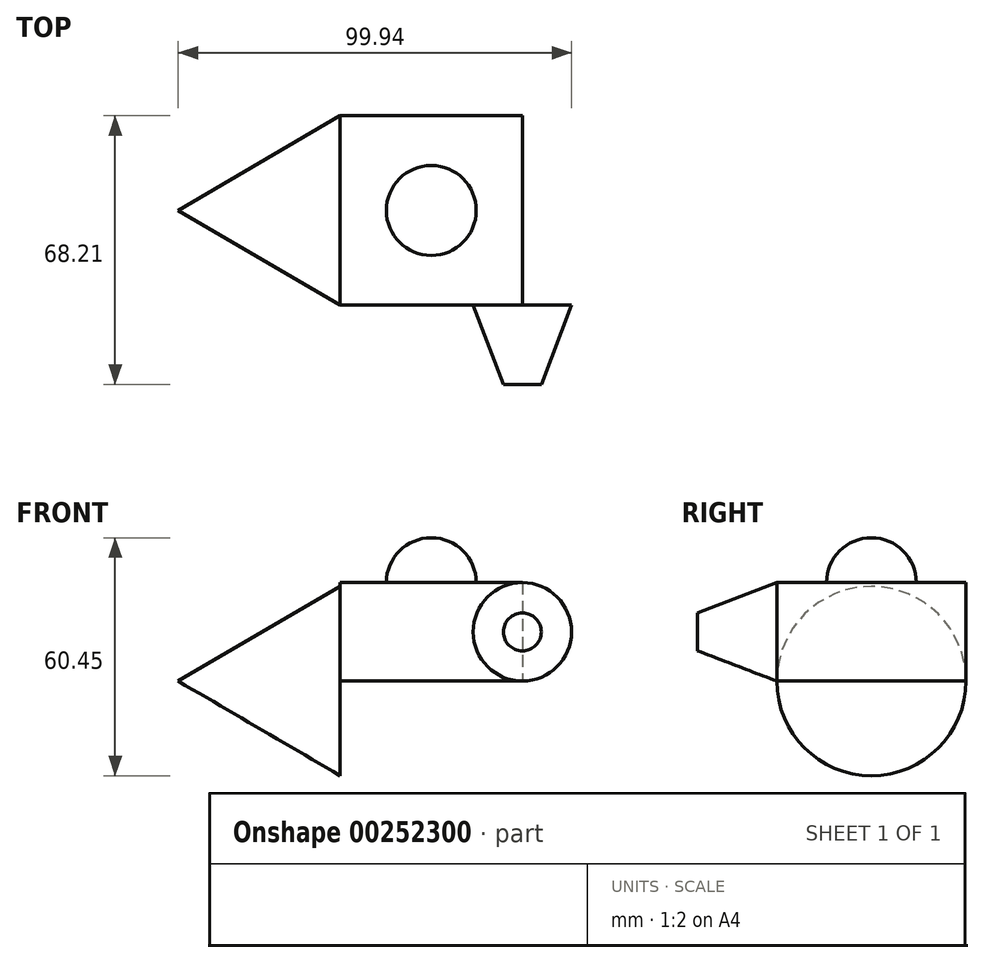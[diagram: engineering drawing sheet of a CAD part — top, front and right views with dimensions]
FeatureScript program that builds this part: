
annotation { "Feature Type Name" : "Feature", "Feature Type Description" : "" }
export const myFeature = defineFeature(function(context is Context, id is Id, definition is map)
    precondition{}
    {
        {
            var Q0;
            Q0=qCreatedBy(makeId("Top.planeOp"),FACE);
            var sketch = newSketch(context, id + "F0", { "sketchPlane" : qUnion([Q0])});
            skLineSegment(sketch, "E0.bottom", {"start": v(-23.14, 24.04) * mm, "end": v(23.14, 24.04) * mm});
            skLineSegment(sketch, "E0.top", {"start": v(-23.14, -24.04) * mm, "end": v(23.14, -24.04) * mm});
            skLineSegment(sketch, "E0.left", {"start": v(-23.14, 24.04) * mm, "end": v(-23.14, -24.04) * mm});
            skLineSegment(sketch, "E0.right", {"start": v(23.14, 24.04) * mm, "end": v(23.14, -24.04) * mm});
            skPoint(sketch, "E0.middle", {"position": v(0, 0) * mm});
            skSolve(sketch);
        }
        {
            var Q0;
            Q0=makeQuery(id+"F0.imprint","IMPRINT",FACE,{"disambiguationData":[TD([[makeQuery(id+"F0.imprint","IMPRINT",EDGE,{"derivedFrom":sQuery(id+"F0.wireOp",EDGE,"E0.bottom")}),-1.0]])]});
            extrude(context, id + "F1", {"entities" : qUnion([Q0]), "endBound" : BoundingType.SYMMETRIC, "depth" : 25 * mm});
        }
        {
            var Q0;
            Q0=makeQuery(id+"F1.opExtrude","CAP_FACE",FACE,{"disambiguationData":[OSD([sQuery(id+"F0.wireOp",EDGE,"E0.bottom"),sQuery(id+"F0.wireOp",EDGE,"E0.top"),sQuery(id+"F0.wireOp",EDGE,"E0.left"),sQuery(id+"F0.wireOp",EDGE,"E0.right")])],"isStart":false});
            var sketch = newSketch(context, id + "F2", { "sketchPlane" : qUnion([Q0])});
            skArc(sketch, "E1", {"start": v(-11.41, 0) * mm, "mid": v(0, -11.41) * mm, "end": v(11.41, 0) * mm});
            skLineSegment(sketch, "E2", {"start": v(0, 0) * mm, "end": v(11.41, 0) * mm});
            skLineSegment(sketch, "E3", {"start": v(11.41, 0) * mm, "end": v(-11.41, 0) * mm});
            skLineSegment(sketch, "E4", {"start": v(23.14, 0) * mm, "end": v(-23.14, 0) * mm, "construction": true});
            skSolve(sketch);
        }
        {
            var Q0;
            Q0 = qSketchRegion(id + "F2", true);
            var Q1;
            Q1=sQuery(id+"F2.wireOp",EDGE,"E4");
            revolve(context, id + "F3", {"operationType" : NewBodyOperationType.ADD, "entities" : qUnion([Q0]), "axis" : qUnion([Q1]), "revolveType" : RevolveType.FULL});
        }
        {
            var Q0;
            Q0=makeQuery(id+"F1.opExtrude","CAP_FACE",FACE,{"disambiguationData":[OSD([sQuery(id+"F0.wireOp",EDGE,"E0.bottom"),sQuery(id+"F0.wireOp",EDGE,"E0.top"),sQuery(id+"F0.wireOp",EDGE,"E0.left"),sQuery(id+"F0.wireOp",EDGE,"E0.right")])],"isStart":true});
            var sketch = newSketch(context, id + "F4", { "sketchPlane" : qUnion([Q0])});
            skLineSegment(sketch, "E5", {"start": v(-23.14, -24.04) * mm, "end": v(-64.3, 0) * mm});
            skLineSegment(sketch, "E6", {"start": v(-64.3, 0) * mm, "end": v(-23.14, 0) * mm});
            skLineSegment(sketch, "E7", {"start": v(-23.14, 0) * mm, "end": v(-23.14, -24.04) * mm});
            skSolve(sketch);
        }
        {
            var Q0;
            Q0 = qSketchRegion(id + "F4", true);
            var Q1;
            Q1=sQuery(id+"F4.wireOp",EDGE,"E6");
            revolve(context, id + "F5", {"operationType" : NewBodyOperationType.ADD, "entities" : qUnion([Q0]), "axis" : qUnion([Q1]), "revolveType" : RevolveType.FULL});
        }
        {
            var Q0;
            Q0=makeQuery(id+"F1.opExtrude","SWEPT_FACE",FACE,{"disambiguationData":[OSD([sQuery(id+"F0.wireOp",EDGE,"E0.right")])]});
            var sketch = newSketch(context, id + "F6", { "sketchPlane" : qUnion([Q0])});
            skLineSegment(sketch, "E8", {"start": v(-24.04, -12.5) * mm, "end": v(-44.17, -4.8) * mm});
            skLineSegment(sketch, "E9", {"start": v(-44.17, -4.8) * mm, "end": v(-44.17, 0) * mm});
            skLineSegment(sketch, "E10", {"start": v(-44.17, 0) * mm, "end": v(-24.04, 0) * mm});
            skLineSegment(sketch, "E11", {"start": v(-24.04, 0) * mm, "end": v(-24.04, -12.5) * mm});
            skSolve(sketch);
        }
        {
            var Q0;
            Q0 = qSketchRegion(id + "F6", true);
            var Q1;
            Q1=sQuery(id+"F6.wireOp",EDGE,"E10");
            revolve(context, id + "F7", {"operationType" : NewBodyOperationType.ADD, "entities" : qUnion([Q0]), "axis" : qUnion([Q1]), "revolveType" : RevolveType.FULL});
        }
    });
